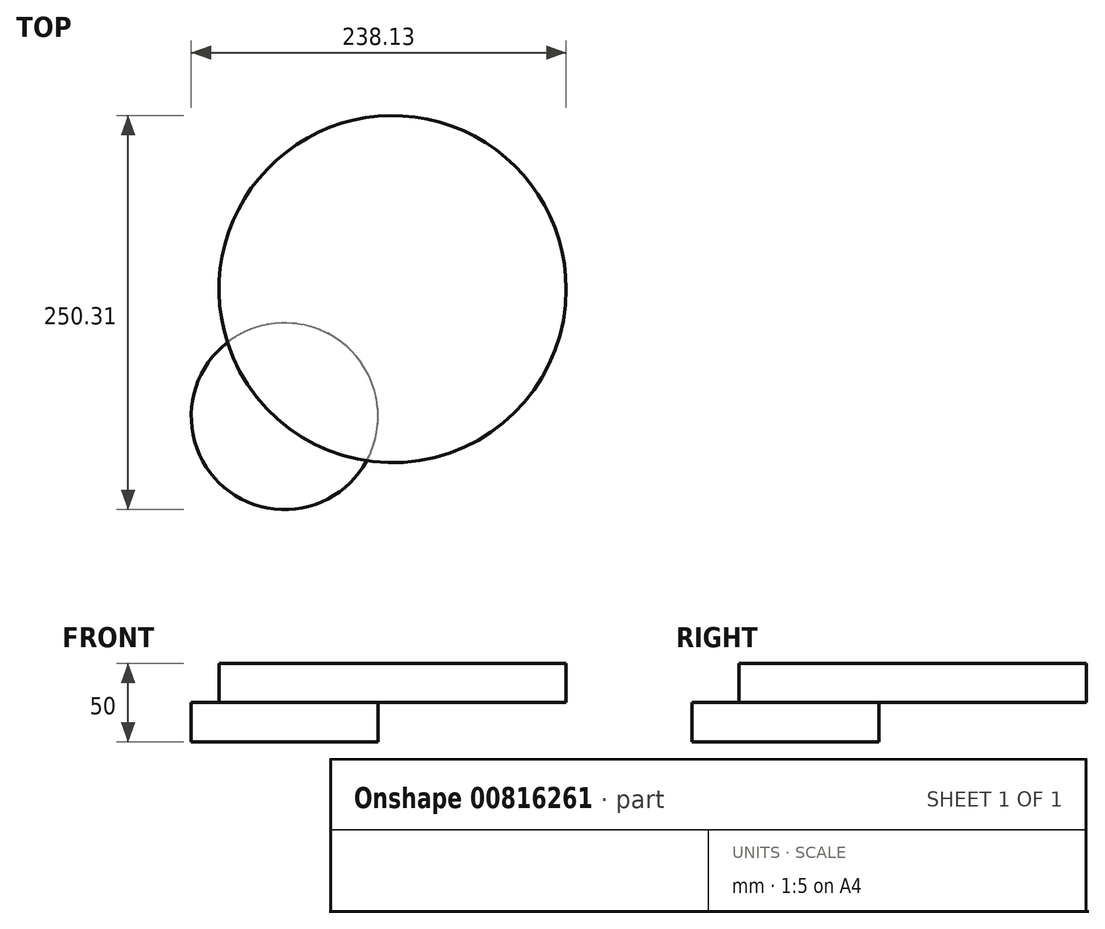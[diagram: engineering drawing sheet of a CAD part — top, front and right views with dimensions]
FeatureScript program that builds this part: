
annotation { "Feature Type Name" : "Feature", "Feature Type Description" : "" }
export const myFeature = defineFeature(function(context is Context, id is Id, definition is map)
    precondition{}
    {
        {
            var Q0;
            Q0=qCreatedBy(makeId("Top.planeOp"),FACE);
            var sketch = newSketch(context, id + "F0", { "sketchPlane" : qUnion([Q0])});
            skCircle(sketch, "E0", {"center": v(0, 5.6) * mm, "radius": 59.33 * mm});
            skPoint(sketch, "E1.center.orphan", {"position": v(0, 0) * mm});
            skSolve(sketch);
        }
        {
            var Q0;
            Q0 = qSketchRegion(id + "F0", true);
            extrude(context, id + "F1", {"entities" : qUnion([Q0]), "depth" : 25 * mm, "offsetDistance" : 25 * mm});
        }
        {
            var Q0;
            Q0=makeQuery(id+"F1.opExtrude","CAP_FACE",FACE,{"disambiguationData":[OSD([sQuery(id+"F0.wireOp",EDGE,"E0")])],"isStart":false});
            var sketch = newSketch(context, id + "F2", { "sketchPlane" : qUnion([Q0])});
            skCircle(sketch, "E2", {"center": v(68.55, 86.34) * mm, "radius": 110.25 * mm});
            skPoint(sketch, "E2.first.point", {"position": v(-14.4, 13.71) * mm});
            skPoint(sketch, "E2.second.point", {"position": v(0, 0) * mm});
            skPoint(sketch, "E2.third.point", {"position": v(-25.73, 29.2) * mm});
            skSolve(sketch);
        }
        {
            var Q0;
            Q0 = qSketchRegion(id + "F2", true);
            extrude(context, id + "F3", {"entities" : qUnion([Q0]), "operationType" : NewBodyOperationType.ADD, "depth" : 25 * mm, "offsetDistance" : 25 * mm});
        }
    });
